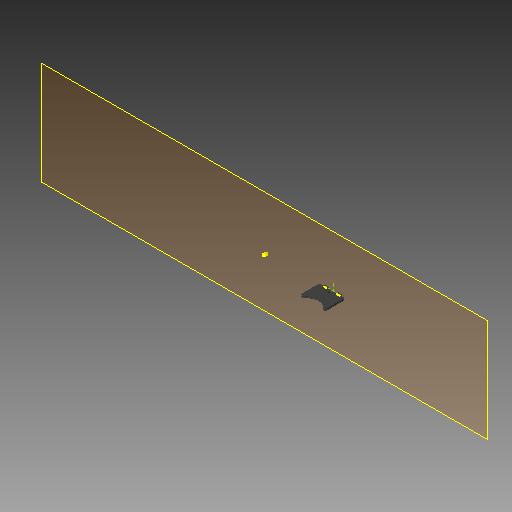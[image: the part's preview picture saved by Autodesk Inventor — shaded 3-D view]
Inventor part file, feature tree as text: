
AUTODESK INVENTOR PART (.ipt)
format: ipt  version: 2018 (Build 220112000, 112)  size: 194,048 bytes
history: native  units: mm
features: sketch x7, extrude x6, fillet x2, reference x2, projected_geometry x2, other x2, plane x1
ambient origin geometry x8: Origin, YZ Plane, XZ Plane, XY Plane, X Axis, Y Axis, Z Axis, Center Point
bodies: Solid1 (feature_tree)
feature tree (22):
  plane  "Work Plane1"
  extrude  "Extrusion1"  Depth=3.0mm
  sketch  "Sketch2"  dims[d2=6.0mm d3=3.0mm]
  extrude  "Extrusion2"  Depth=3.0mm
  extrude  "Extrusion3"  Depth=40.0mm
  fillet  "Fillet1"  Radius=3.0mm
  extrude  "Extrusion4"  Depth=40.0mm
  fillet  "Fillet2"  Radius=38.0mm
  extrude  "Extrusion5"  Depth=16.0mm
  sketch  "Sketch7"  dims[d17=2.0mm d18=40.0mm d19=0.0mm d20=2.0mm d21=1.5mm d22=10.7mm d23=1.5mm d24=6.0mm d25=1.2mm d26=2.0mm d27=40.0mm d28=0.0mm]
  sketch  "Sketch1"  dims[d0=6.0mm d1=3.0mm]
  reference  "Reference1"
  reference  "Reference2"
  projected_geometry  "Projected Loop1"
  projected_geometry  "Projected Loop2"
  sketch  "Sketch3"  dims[d4=3.0mm d5=0.0mm d6=40.0mm d7=3.0mm]
  sketch  "Sketch4"  dims[d8=60.0mm d9=0.0mm d10=40.0mm d11=38.0mm]
  sketch  "Sketch5"  dims[d12=16.0mm d13=16.0mm]
  sketch  "Sketch6"  dims[d14=3.2mm d15=40.0mm d16=0.0mm]
  other  "<userpath>\OneDrive\Inventor\Beast 3D Printer\Extruder Assembly.iam"
  extrude  "Extruder Assembly.iam"  Depth=40.0mm TaperAngle=0.0deg
  other  "Rear Extruder Panel:1"
